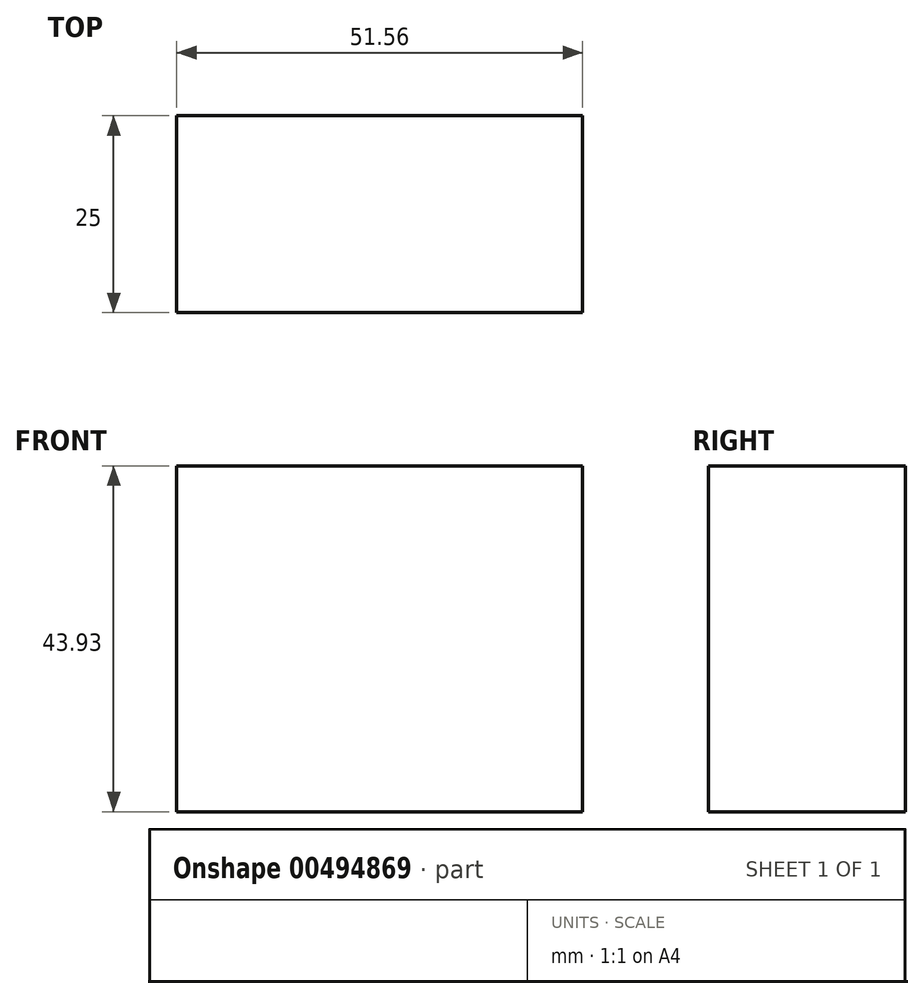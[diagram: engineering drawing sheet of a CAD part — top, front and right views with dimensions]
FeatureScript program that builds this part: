
annotation { "Feature Type Name" : "Feature", "Feature Type Description" : "" }
export const myFeature = defineFeature(function(context is Context, id is Id, definition is map)
    precondition{}
    {
        {
            var Q0;
            Q0=qCreatedBy(makeId("Front.planeOp"),FACE);
            var sketch = newSketch(context, id + "F0", { "sketchPlane" : qUnion([Q0])});
            skLineSegment(sketch, "E0.bottom", {"start": v(0, 0) * mm, "end": v(-51.56, 0) * mm});
            skLineSegment(sketch, "E0.top", {"start": v(0, 43.93) * mm, "end": v(-51.56, 43.93) * mm});
            skLineSegment(sketch, "E0.left", {"start": v(0, 0) * mm, "end": v(0, 43.93) * mm});
            skLineSegment(sketch, "E0.right", {"start": v(-51.56, 0) * mm, "end": v(-51.56, 43.93) * mm});
            skSolve(sketch);
        }
        {
            var Q0;
            Q0 = qSketchRegion(id + "F0", true);
            extrude(context, id + "F1", {"entities" : qUnion([Q0]), "oppositeDirection" : true, "depth" : 25 * mm});
        }
    });
